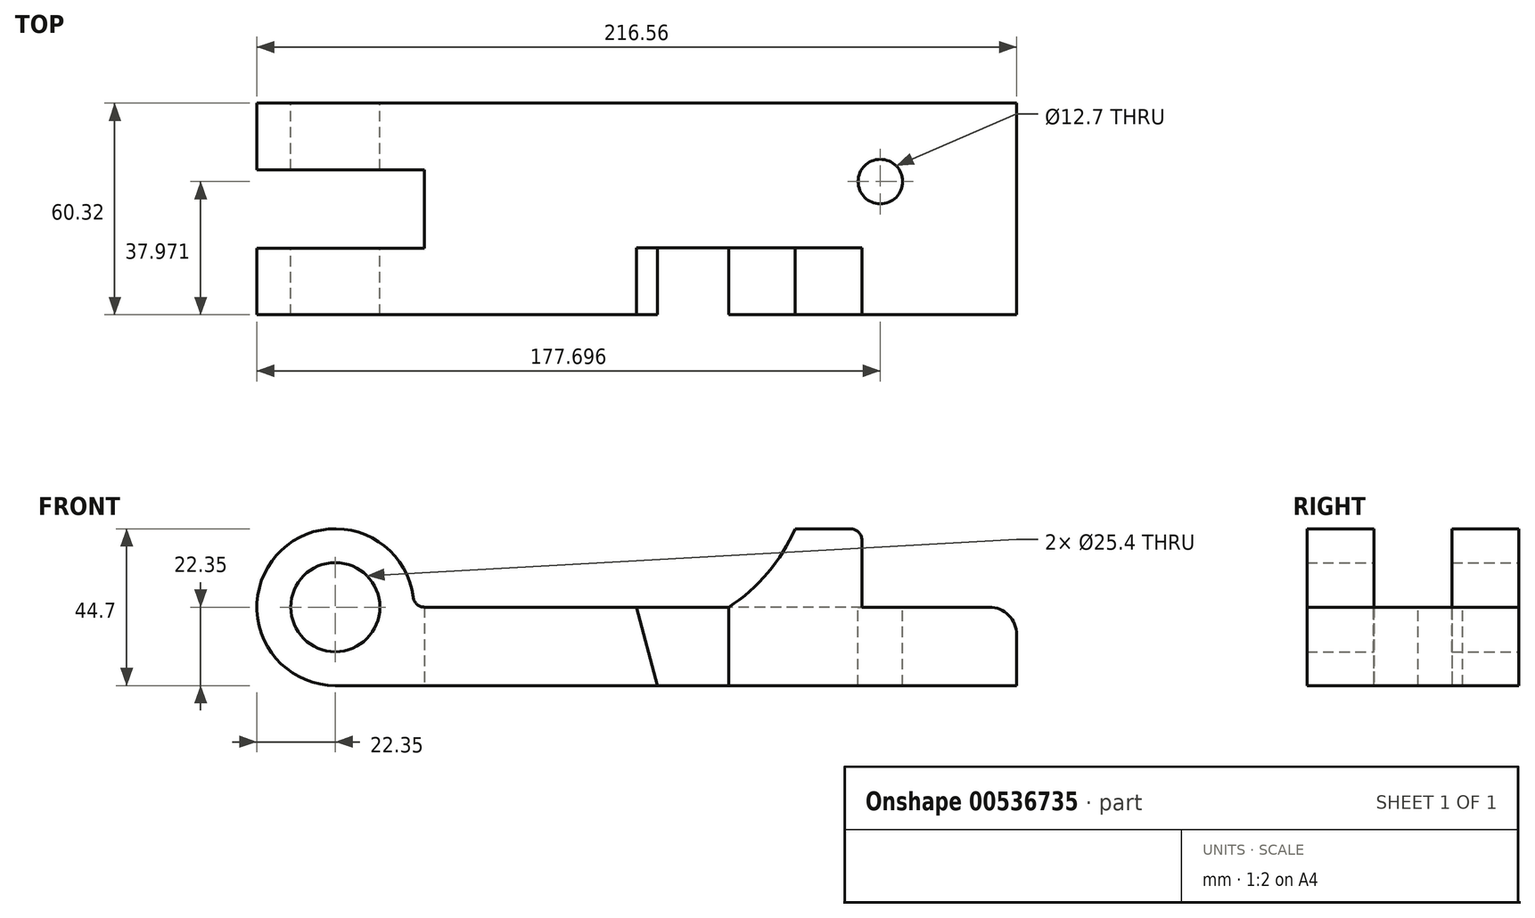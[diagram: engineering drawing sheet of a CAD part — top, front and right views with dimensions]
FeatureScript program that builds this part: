
annotation { "Feature Type Name" : "Feature", "Feature Type Description" : "" }
export const myFeature = defineFeature(function(context is Context, id is Id, definition is map)
    precondition{}
    {
        {
            var Q0;
            Q0=qCreatedBy(makeId("Front.planeOp"),FACE);
            var sketch = newSketch(context, id + "F0", { "sketchPlane" : qUnion([Q0])});
            skCircle(sketch, "E0", {"center": v(0, 0) * mm, "radius": 12.7 * mm});
            skArc(sketch, "E1", {"start": v(22.35, 0) * mm, "mid": v(-15.8, 15.8) * mm, "end": v(0, -22.35) * mm});
            skLineSegment(sketch, "E2", {"start": v(0, -22.35) * mm, "end": v(194.2, -22.35) * mm});
            skLineSegment(sketch, "E3", {"start": v(194.2, -22.35) * mm, "end": v(194.2, 0) * mm});
            skLineSegment(sketch, "E4", {"start": v(194.2, 0) * mm, "end": v(22.35, 0) * mm});
            skSolve(sketch);
        }
        {
            var Q0;
            Q0=makeQuery(id+"F0.imprint","IMPRINT",FACE,{"disambiguationData":[TD([[makeQuery(id+"F0.imprint","IMPRINT",EDGE,{"derivedFrom":sQuery(id+"F0.wireOp",EDGE,"E0")}),-1.0]])]});
            extrude(context, id + "F1", {"entities" : qUnion([Q0]), "endBound" : BoundingType.SYMMETRIC, "depth" : 60.32 * mm, "offsetDistance" : 25.4 * mm});
        }
        {
            var Q0;
            Q0=makeQuery(id+"F1.opExtrude","CAP_FACE",FACE,{"disambiguationData":[OSD([sQuery(id+"F0.wireOp",EDGE,"E0"),sQuery(id+"F0.wireOp",EDGE,"E1"),sQuery(id+"F0.wireOp",EDGE,"E2"),sQuery(id+"F0.wireOp",EDGE,"E3"),sQuery(id+"F0.wireOp",EDGE,"E4")])],"isStart":false});
            var sketch = newSketch(context, id + "F2", { "sketchPlane" : qUnion([Q0])});
            skArc(sketch, "E5.0", {"start": v(22.35, 0) * mm, "mid": v(-15.8, 15.8) * mm, "end": v(0, -22.35) * mm});
            skCircle(sketch, "E5.1", {"center": v(0, 0) * mm, "radius": 12.7 * mm});
            skLineSegment(sketch, "E6.0", {"start": v(0, -22.35) * mm, "end": v(194.2, -22.35) * mm});
            skPoint(sketch, "E7.0", {"position": v(194.2, -11.18) * mm});
            skLineSegment(sketch, "E8.0", {"start": v(194.2, -22.35) * mm, "end": v(194.2, 0) * mm});
            skLineSegment(sketch, "E9.0", {"start": v(194.2, 0) * mm, "end": v(22.35, 0) * mm});
            skLineSegment(sketch, "E10", {"start": v(0, -22.35) * mm, "end": v(91.85, -22.35) * mm});
            skLineSegment(sketch, "E11", {"start": v(85.85, 0) * mm, "end": v(91.85, -22.35) * mm});
            skLineSegment(sketch, "E12", {"start": v(0, -22.35) * mm, "end": v(112.17, -22.35) * mm});
            skLineSegment(sketch, "E13", {"start": v(112.17, -22.35) * mm, "end": v(112.17, 0) * mm});
            skLineSegment(sketch, "E14", {"start": v(85.85, 0) * mm, "end": v(112.17, 0) * mm});
            skLineSegment(sketch, "E15", {"start": v(0, 22.35) * mm, "end": v(131.04, 22.35) * mm, "construction": true});
            skLineSegment(sketch, "E16", {"start": v(131.04, 22.35) * mm, "end": v(150.09, 22.35) * mm});
            skLineSegment(sketch, "E17", {"start": v(150.09, 22.35) * mm, "end": v(150.09, 0) * mm});
            skLineSegment(sketch, "E18", {"start": v(150.09, 0) * mm, "end": v(131.04, 0) * mm});
            skLineSegment(sketch, "E19", {"start": v(112.17, 0) * mm, "end": v(131.04, 0) * mm});
            skArc(sketch, "E20", {"start": v(112.17, 0) * mm, "mid": v(123.25, 9.79) * mm, "end": v(131.04, 22.35) * mm});
            skSolve(sketch);
        }
        {
            var Q0;
            Q0=makeQuery(id+"F1.opExtrude","SWEPT_EDGE",EDGE,{"disambiguationData":[OSD([sQuery(id+"F0.wireOp",EDGE,"E1"),sQuery(id+"F0.wireOp",EDGE,"E4")])]});
            fillet(context, id + "F3", {"entities" : qUnion([Q0]), "radius" : 3.3 * mm, "tangentPropagation" : true, "allowEdgeOverflow" : false});
        }
        {
            var Q0;
            Q0=makeQuery(id+"F1.opExtrude","SWEPT_EDGE",EDGE,{"disambiguationData":[OSD([sQuery(id+"F0.wireOp",EDGE,"E3"),sQuery(id+"F0.wireOp",EDGE,"E4")])]});
            fillet(context, id + "F4", {"entities" : qUnion([Q0]), "radius" : 7.87 * mm, "tangentPropagation" : true, "allowEdgeOverflow" : false});
        }
        {
            var Q0;
            {var subQ0=sQuery(id+"F2.wireOp",EDGE,"E11");Q0=makeQuery(id+"F2.imprint","IMPRINT",FACE,{"disambiguationData":[TD([[makeQuery(id+"F2.imprint","IMPRINT",EDGE,{"derivedFrom":subQ0}),1.0]])]});}
            extrude(context, id + "F5", {"entities" : qUnion([Q0]), "operationType" : NewBodyOperationType.REMOVE, "oppositeDirection" : true, "depth" : 19.05 * mm, "offsetDistance" : 25.4 * mm});
        }
        {
            var Q0;
            Q0=makeQuery(id+"F2.imprint","IMPRINT",FACE,{"disambiguationData":[TD([[makeQuery(id+"F2.imprint","IMPRINT",EDGE,{"derivedFrom":sQuery(id+"F2.wireOp",EDGE,"E16")}),-1.0]])]});
            extrude(context, id + "F6", {"entities" : qUnion([Q0]), "operationType" : NewBodyOperationType.ADD, "depth" : -19.05 * mm, "offsetDistance" : 25.4 * mm});
        }
        {
            var Q0;
            Q0=makeQuery(id+"F6.opExtrude","SWEPT_EDGE",EDGE,{"disambiguationData":[OSD([sQuery(id+"F2.wireOp",EDGE,"E9.0"),sQuery(id+"F2.wireOp",EDGE,"E17"),sQuery(id+"F2.wireOp",EDGE,"E18")])]});
            var Q1;
            Q1=makeQuery(id+"F6.opExtrude","SWEPT_EDGE",EDGE,{"disambiguationData":[OSD([sQuery(id+"F2.wireOp",EDGE,"E16"),sQuery(id+"F2.wireOp",EDGE,"E17")])]});
            fillet(context, id + "F7", {"entities" : qUnion([Q0, Q1]), "radius" : 3.3 * mm, "tangentPropagation" : true, "allowEdgeOverflow" : false});
        }
        {
            var Q0;
            Q0=qCreatedBy(makeId("Front.planeOp"),FACE);
            var sketch = newSketch(context, id + "F8", { "sketchPlane" : qUnion([Q0])});
            skCircle(sketch, "E21.10", {"center": v(0, 0) * mm, "radius": 12.7 * mm});
            skArc(sketch, "E21.11", {"start": v(22.17, 2.88) * mm, "mid": v(-16.8, 14.75) * mm, "end": v(0, -22.35) * mm});
            skArc(sketch, "E21.13", {"start": v(22.17, 2.88) * mm, "mid": v(-16.8, 14.75) * mm, "end": v(0, -22.35) * mm});
            skArc(sketch, "E21.20", {"start": v(22.17, 2.88) * mm, "mid": v(-16.8, 14.75) * mm, "end": v(0, -22.35) * mm});
            skCircle(sketch, "E21.21", {"center": v(0, 0) * mm, "radius": 12.7 * mm});
            skArc(sketch, "E22.0.2", {"start": v(25.44, 0) * mm, "mid": v(23.26, 0.82) * mm, "end": v(22.17, 2.88) * mm});
            skLineSegment(sketch, "E23", {"start": v(25.44, 0) * mm, "end": v(25.44, -22.35) * mm});
            skLineSegment(sketch, "E24", {"start": v(0, -22.35) * mm, "end": v(25.44, -22.35) * mm});
            skPoint(sketch, "E25.orphan", {"position": v(22.35, 0) * mm});
            skSolve(sketch);
        }
        {
            var Q0;
            Q0 = qSketchRegion(id + "F8", true);
            extrude(context, id + "F9", {"entities" : qUnion([Q0]), "operationType" : NewBodyOperationType.REMOVE, "endBound" : BoundingType.SYMMETRIC, "oppositeDirection" : true, "depth" : 22.33 * mm, "offsetDistance" : 25.4 * mm});
        }
        {
            var Q0;
            Q0=makeQuery(id+"F1.opExtrude","SWEPT_FACE",FACE,{"disambiguationData":[OSD([sQuery(id+"F0.wireOp",EDGE,"E4")])]});
            var sketch = newSketch(context, id + "F10", { "sketchPlane" : qUnion([Q0])});
            skLineSegment(sketch, "E26.0", {"start": v(194.2, 30.16) * mm, "end": v(194.2, -30.16) * mm});
            skLineSegment(sketch, "E27.0", {"start": v(186.33, -30.16) * mm, "end": v(186.33, 30.16) * mm});
            skLineSegment(sketch, "E28.0", {"start": v(186.33, 30.16) * mm, "end": v(25.44, 30.16) * mm});
            skPoint(sketch, "E29.0", {"position": v(191.9, 30.16) * mm});
            skLineSegment(sketch, "E30.0", {"start": v(186.33, 30.16) * mm, "end": v(194.2, 30.16) * mm});
            skLineSegment(sketch, "E31.0", {"start": v(194.2, -30.16) * mm, "end": v(186.33, -30.16) * mm});
            skLineSegment(sketch, "E32.0", {"start": v(186.33, -30.16) * mm, "end": v(153.4, -30.16) * mm});
            skLineSegment(sketch, "E33", {"start": v(194.2, 30.16) * mm, "end": v(155.35, 30.16) * mm});
            skLineSegment(sketch, "E34", {"start": v(155.35, 30.16) * mm, "end": v(155.35, 7.81) * mm});
            skCircle(sketch, "E35", {"center": v(155.35, 7.81) * mm, "radius": 6.35 * mm});
            skSolve(sketch);
        }
        {
            var Q0;
            Q0=makeQuery(id+"F10.imprint","IMPRINT",FACE,{"disambiguationData":[TD([[makeQuery(id+"F10.imprint","IMPRINT",EDGE,{"derivedFrom":sQuery(id+"F10.wireOp",EDGE,"E35")}),1.0]])]});
            extrude(context, id + "F11", {"entities" : qUnion([Q0]), "operationType" : NewBodyOperationType.REMOVE, "oppositeDirection" : true, "depth" : 22.35 * mm, "offsetDistance" : 25.4 * mm});
        }
    });
